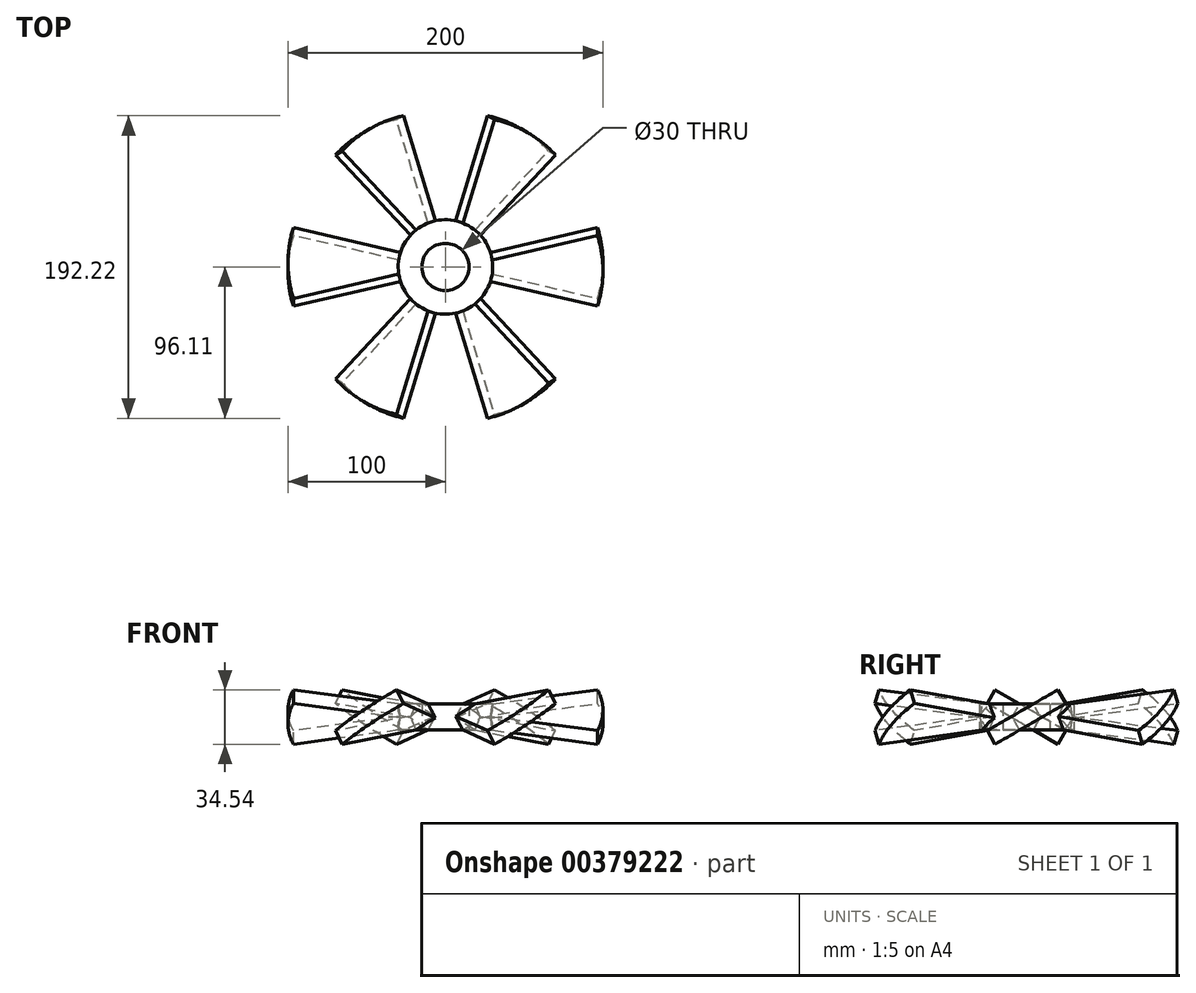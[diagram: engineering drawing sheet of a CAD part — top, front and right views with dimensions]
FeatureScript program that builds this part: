
annotation { "Feature Type Name" : "Feature", "Feature Type Description" : "" }
export const myFeature = defineFeature(function(context is Context, id is Id, definition is map)
    precondition{}
    {
        {
            var Q0;
            Q0=qCreatedBy(makeId("Top.planeOp"),FACE);
            var sketch = newSketch(context, id + "F0", { "sketchPlane" : qUnion([Q0])});
            skLineSegment(sketch, "E0", {"start": v(0, 0) * mm, "end": v(96.6, 25.88) * mm});
            skArc(sketch, "E1", {"start": v(96.6, 25.88) * mm, "mid": v(100, 0) * mm, "end": v(96.6, -25.88) * mm});
            skLineSegment(sketch, "E2", {"start": v(0, 0) * mm, "end": v(145.48, 0) * mm, "construction": true});
            skLineSegment(sketch, "E3.MirrorCS", {"start": v(0, 0) * mm, "end": v(96.6, -25.88) * mm});
            skSolve(sketch);
        }
        {
            var Q0;
            Q0=makeQuery(id+"F0.imprint","IMPRINT",FACE,{"disambiguationData":[TD([[makeQuery(id+"F0.imprint","IMPRINT",EDGE,{"derivedFrom":sQuery(id+"F0.wireOp",EDGE,"E0")}),-1.0]])]});
            extrude(context, id + "F1", {"entities" : qUnion([Q0]), "endBound" : BoundingType.SYMMETRIC, "oppositeDirection" : true, "depth" : 10 * mm});
        }
        {
            var Q0;
            Q0=makeQuery(id+"F1.opExtrude","SWEPT_BODY",BODY,{"disambiguationData":[OSD([sQuery(id+"F0.wireOp",EDGE,"E0"),sQuery(id+"F0.wireOp",EDGE,"E1"),sQuery(id+"F0.wireOp",EDGE,"E3.MirrorCS")])]});
            var Q1;
            Q1=sQuery(id+"F0.wireOp",EDGE,"E2");
            transform(context, id + "F2", {"entities" : qUnion([Q0]), "transformType" : TransformType.ROTATION, "transformAxis" : qUnion([Q1]), "angle" : 30 * degree, "makeCopy" : false});
        }
        {
            var Q0;
            Q0=qCreatedBy(makeId("Right.planeOp"),FACE);
            var sketch = newSketch(context, id + "F3", { "sketchPlane" : qUnion([Q0])});
            skLineSegment(sketch, "E4", {"start": v(0, 23.62) * mm, "end": v(0, -27.4) * mm, "construction": true});
            skSolve(sketch);
        }
        {
            var Q0;
            Q0=makeQuery(id+"F1.opExtrude","SWEPT_BODY",BODY,{"disambiguationData":[OSD([sQuery(id+"F0.wireOp",EDGE,"E0"),sQuery(id+"F0.wireOp",EDGE,"E1"),sQuery(id+"F0.wireOp",EDGE,"E3.MirrorCS")])]});
            var Q1;
            Q1=sQuery(id+"F3.wireOp",EDGE,"E4");
            circularPattern(context, id + "F4", {"entities" : qUnion([Q0]), "axis" : qUnion([Q1]), "angle" : 360 * degree, "instanceCount" : 6, "equalSpace" : true});
        }
        {
            var Q0;
            Q0=qCreatedBy(makeId("Top.planeOp"),FACE);
            var sketch = newSketch(context, id + "F5", { "sketchPlane" : qUnion([Q0])});
            skCircle(sketch, "E5", {"center": v(0, 0) * mm, "radius": 30 * mm});
            skSolve(sketch);
        }
        {
            var Q0;
            Q0=makeQuery(id+"F5.imprint","IMPRINT",FACE,{"disambiguationData":[TD([[makeQuery(id+"F5.imprint","IMPRINT",EDGE,{"derivedFrom":sQuery(id+"F5.wireOp",EDGE,"E5")}),1.0]])]});
            extrude(context, id + "F6", {"entities" : qUnion([Q0]), "endBound" : BoundingType.SYMMETRIC, "depth" : 25 * mm});
        }
        {
            var Q0;
            Q0=makeQuery(id+"F4.opPattern","COPY",BODY,{"derivedFrom":makeQuery(id+"F1.opExtrude","SWEPT_BODY",BODY,{"disambiguationData":[OSD([sQuery(id+"F0.wireOp",EDGE,"E0"),sQuery(id+"F0.wireOp",EDGE,"E1"),sQuery(id+"F0.wireOp",EDGE,"E3.MirrorCS")])]}),"instanceName":"1"});
            var Q1;
            Q1=makeQuery(id+"F4.opPattern","COPY",BODY,{"derivedFrom":makeQuery(id+"F1.opExtrude","SWEPT_BODY",BODY,{"disambiguationData":[OSD([sQuery(id+"F0.wireOp",EDGE,"E0"),sQuery(id+"F0.wireOp",EDGE,"E1"),sQuery(id+"F0.wireOp",EDGE,"E3.MirrorCS")])]}),"instanceName":"2"});
            var Q2;
            Q2=makeQuery(id+"F4.opPattern","COPY",BODY,{"derivedFrom":makeQuery(id+"F1.opExtrude","SWEPT_BODY",BODY,{"disambiguationData":[OSD([sQuery(id+"F0.wireOp",EDGE,"E0"),sQuery(id+"F0.wireOp",EDGE,"E1"),sQuery(id+"F0.wireOp",EDGE,"E3.MirrorCS")])]}),"instanceName":"5"});
            var Q3;
            Q3=makeQuery(id+"F4.opPattern","COPY",BODY,{"derivedFrom":makeQuery(id+"F1.opExtrude","SWEPT_BODY",BODY,{"disambiguationData":[OSD([sQuery(id+"F0.wireOp",EDGE,"E0"),sQuery(id+"F0.wireOp",EDGE,"E1"),sQuery(id+"F0.wireOp",EDGE,"E3.MirrorCS")])]}),"instanceName":"3"});
            var Q4;
            Q4=makeQuery(id+"F1.opExtrude","SWEPT_BODY",BODY,{"disambiguationData":[OSD([sQuery(id+"F0.wireOp",EDGE,"E0"),sQuery(id+"F0.wireOp",EDGE,"E1"),sQuery(id+"F0.wireOp",EDGE,"E3.MirrorCS")])]});
            var Q5;
            Q5=makeQuery(id+"F4.opPattern","COPY",BODY,{"derivedFrom":makeQuery(id+"F1.opExtrude","SWEPT_BODY",BODY,{"disambiguationData":[OSD([sQuery(id+"F0.wireOp",EDGE,"E0"),sQuery(id+"F0.wireOp",EDGE,"E1"),sQuery(id+"F0.wireOp",EDGE,"E3.MirrorCS")])]}),"instanceName":"4"});
            var Q6;
            Q6=makeQuery(id+"F6.opExtrude","SWEPT_BODY",BODY,{"disambiguationData":[OSD([sQuery(id+"F5.wireOp",EDGE,"E5")])]});
            booleanBodies(context, id + "F7", {"operationType" : BooleanOperationType.UNION, "tools" : qUnion([Q0, Q1, Q2, Q3, Q4, Q5, Q6])});
        }
        {
            var Q0;
            {var subQ0=sQuery(id+"F0.wireOp",EDGE,"E0");Q0=makeQuery(id+"F7.opBoolean","INTERSECT",VERTEX,{"derivedFrom":[makeQuery(id+"F4.opPattern","COPY",FACE,{"derivedFrom":makeQuery(id+"F1.opExtrude","SWEPT_FACE",FACE,{"disambiguationData":[OSD([subQ0])]}),"instanceName":"1"}),makeQuery(id+"F4.opPattern","COPY",FACE,{"derivedFrom":makeQuery(id+"F1.opExtrude","CAP_FACE",FACE,{"disambiguationData":[OSD([subQ0,sQuery(id+"F0.wireOp",EDGE,"E1"),sQuery(id+"F0.wireOp",EDGE,"E3.MirrorCS")])],"isStart":true}),"instanceName":"1"}),makeQuery(id+"F6.opExtrude","SWEPT_FACE",FACE,{"disambiguationData":[OSD([sQuery(id+"F5.wireOp",EDGE,"E5")])]})]});}
            var Q1;
            {var subQ0=sQuery(id+"F0.wireOp",EDGE,"E0");Q1=makeQuery(id+"F7.opBoolean","INTERSECT",VERTEX,{"derivedFrom":[makeQuery(id+"F4.opPattern","COPY",FACE,{"derivedFrom":makeQuery(id+"F1.opExtrude","SWEPT_FACE",FACE,{"disambiguationData":[OSD([subQ0])]}),"instanceName":"2"}),makeQuery(id+"F4.opPattern","COPY",FACE,{"derivedFrom":makeQuery(id+"F1.opExtrude","CAP_FACE",FACE,{"disambiguationData":[OSD([subQ0,sQuery(id+"F0.wireOp",EDGE,"E1"),sQuery(id+"F0.wireOp",EDGE,"E3.MirrorCS")])],"isStart":true}),"instanceName":"2"}),makeQuery(id+"F6.opExtrude","SWEPT_FACE",FACE,{"disambiguationData":[OSD([sQuery(id+"F5.wireOp",EDGE,"E5")])]})]});}
            var Q2;
            {var subQ0=sQuery(id+"F0.wireOp",EDGE,"E0");Q2=makeQuery(id+"F7.opBoolean","INTERSECT",VERTEX,{"derivedFrom":[makeQuery(id+"F4.opPattern","COPY",FACE,{"derivedFrom":makeQuery(id+"F1.opExtrude","SWEPT_FACE",FACE,{"disambiguationData":[OSD([subQ0])]}),"instanceName":"5"}),makeQuery(id+"F4.opPattern","COPY",FACE,{"derivedFrom":makeQuery(id+"F1.opExtrude","CAP_FACE",FACE,{"disambiguationData":[OSD([subQ0,sQuery(id+"F0.wireOp",EDGE,"E1"),sQuery(id+"F0.wireOp",EDGE,"E3.MirrorCS")])],"isStart":true}),"instanceName":"5"}),makeQuery(id+"F6.opExtrude","SWEPT_FACE",FACE,{"disambiguationData":[OSD([sQuery(id+"F5.wireOp",EDGE,"E5")])]})]});}
            cPlane(context, id + "F8", {"entities" : qUnion([Q0, Q1, Q2]), "cplaneType" : CPlaneType.THREE_POINT, "offset" : 25 * mm, "width" : 150 * mm, "height" : 150 * mm});
        }
        {
            var Q0;
            {var subQ0=sQuery(id+"F0.wireOp",EDGE,"E3.MirrorCS");Q0=makeQuery(id+"F7.opBoolean","INTERSECT",VERTEX,{"derivedFrom":[makeQuery(id+"F1.opExtrude","CAP_FACE",FACE,{"disambiguationData":[OSD([sQuery(id+"F0.wireOp",EDGE,"E0"),sQuery(id+"F0.wireOp",EDGE,"E1"),subQ0])],"isStart":false}),makeQuery(id+"F1.opExtrude","SWEPT_FACE",FACE,{"disambiguationData":[OSD([subQ0])]}),makeQuery(id+"F6.opExtrude","SWEPT_FACE",FACE,{"disambiguationData":[OSD([sQuery(id+"F5.wireOp",EDGE,"E5")])]})]});}
            var Q1;
            {var subQ0=sQuery(id+"F0.wireOp",EDGE,"E3.MirrorCS");Q1=makeQuery(id+"F7.opBoolean","INTERSECT",VERTEX,{"derivedFrom":[makeQuery(id+"F4.opPattern","COPY",FACE,{"derivedFrom":makeQuery(id+"F1.opExtrude","CAP_FACE",FACE,{"disambiguationData":[OSD([sQuery(id+"F0.wireOp",EDGE,"E0"),sQuery(id+"F0.wireOp",EDGE,"E1"),subQ0])],"isStart":false}),"instanceName":"2"}),makeQuery(id+"F4.opPattern","COPY",FACE,{"derivedFrom":makeQuery(id+"F1.opExtrude","SWEPT_FACE",FACE,{"disambiguationData":[OSD([subQ0])]}),"instanceName":"2"}),makeQuery(id+"F6.opExtrude","SWEPT_FACE",FACE,{"disambiguationData":[OSD([sQuery(id+"F5.wireOp",EDGE,"E5")])]})]});}
            var Q2;
            {var subQ0=sQuery(id+"F0.wireOp",EDGE,"E3.MirrorCS");Q2=makeQuery(id+"F7.opBoolean","INTERSECT",VERTEX,{"derivedFrom":[makeQuery(id+"F4.opPattern","COPY",FACE,{"derivedFrom":makeQuery(id+"F1.opExtrude","CAP_FACE",FACE,{"disambiguationData":[OSD([sQuery(id+"F0.wireOp",EDGE,"E0"),sQuery(id+"F0.wireOp",EDGE,"E1"),subQ0])],"isStart":false}),"instanceName":"4"}),makeQuery(id+"F4.opPattern","COPY",FACE,{"derivedFrom":makeQuery(id+"F1.opExtrude","SWEPT_FACE",FACE,{"disambiguationData":[OSD([subQ0])]}),"instanceName":"4"}),makeQuery(id+"F6.opExtrude","SWEPT_FACE",FACE,{"disambiguationData":[OSD([sQuery(id+"F5.wireOp",EDGE,"E5")])]})]});}
            cPlane(context, id + "F9", {"entities" : qUnion([Q0, Q1, Q2]), "cplaneType" : CPlaneType.THREE_POINT, "offset" : 25 * mm, "width" : 150 * mm, "height" : 150 * mm});
        }
        {
            var Q0;
            Q0=makeQuery(id+"F6.opExtrude","CAP_FACE",FACE,{"disambiguationData":[OSD([sQuery(id+"F5.wireOp",EDGE,"E5")])],"isStart":true});
            var Q1;
            Q1=qCreatedBy(id+"F9.planeOp",FACE);
            extrude(context, id + "F10", {"entities" : qUnion([Q0]), "operationType" : NewBodyOperationType.REMOVE, "endBound" : BoundingType.UP_TO_SURFACE, "oppositeDirection" : true, "endBoundEntityFace" : qUnion([Q1]), "depth" : 25 * mm});
        }
        {
            var Q0;
            Q0=makeQuery(id+"F6.opExtrude","CAP_FACE",FACE,{"disambiguationData":[OSD([sQuery(id+"F5.wireOp",EDGE,"E5")])],"isStart":false});
            var Q1;
            Q1=qCreatedBy(id+"F8.planeOp",FACE);
            extrude(context, id + "F11", {"entities" : qUnion([Q0]), "operationType" : NewBodyOperationType.REMOVE, "endBound" : BoundingType.UP_TO_SURFACE, "oppositeDirection" : true, "endBoundEntityFace" : qUnion([Q1]), "depth" : 25 * mm});
        }
        {
            var Q0;
            Q0=qCreatedBy(id+"F9.planeOp",FACE);
            var sketch = newSketch(context, id + "F12", { "sketchPlane" : qUnion([Q0])});
            skCircle(sketch, "E6", {"center": v(0, 0) * mm, "radius": 15 * mm});
            skSolve(sketch);
        }
        {
            var Q0;
            Q0=makeQuery(id+"F12.imprint","IMPRINT",FACE,{"disambiguationData":[TD([[makeQuery(id+"F12.imprint","IMPRINT",EDGE,{"derivedFrom":sQuery(id+"F12.wireOp",EDGE,"E6")}),1.0]])]});
            extrude(context, id + "F13", {"entities" : qUnion([Q0]), "operationType" : NewBodyOperationType.REMOVE, "endBound" : BoundingType.UP_TO_NEXT, "depth" : 25 * mm});
        }
    });
